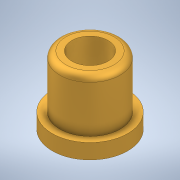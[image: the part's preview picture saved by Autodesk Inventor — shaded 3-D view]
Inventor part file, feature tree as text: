
AUTODESK INVENTOR PART (.ipt)
format: ipt  version: 2022 (Build 260153000, 153)  size: 134,144 bytes
history: native  units: mm
features: extrude x3, sketch x3, fillet x1
ambient origin geometry x8: Origin, YZ Plane, XZ Plane, XY Plane, X Axis, Y Axis, Z Axis, Center Point
bodies: Solid1 (feature_tree)
feature tree (7):
  extrude  "Extrusion1"  Depth=22.5mm TaperAngle=0.0deg
  extrude  "Extrusion2"  TaperAngle=0.0deg  [1 undecoded]
  extrude  "Extrusion3"  Depth=5.0mm TaperAngle=0.0deg
  fillet  "Fillet1"  Radius=2.0mm
  sketch  "Sketch1"  dims[d0=20.0mm d1=22.5mm d2=0.0mm]
  sketch  "Sketch2"  dims[d3=12.0mm d4=0.0mm d5=0.0mm]
  sketch  "Sketch3"  dims[d6=25.0mm d7=5.0mm d8=0.0mm d9=2.0mm]
note: 1 required parameter value undecoded (feature->parameter linkage not recoverable at this tier; creation-order binding heuristic only, values carry confidence <= 0.55)
